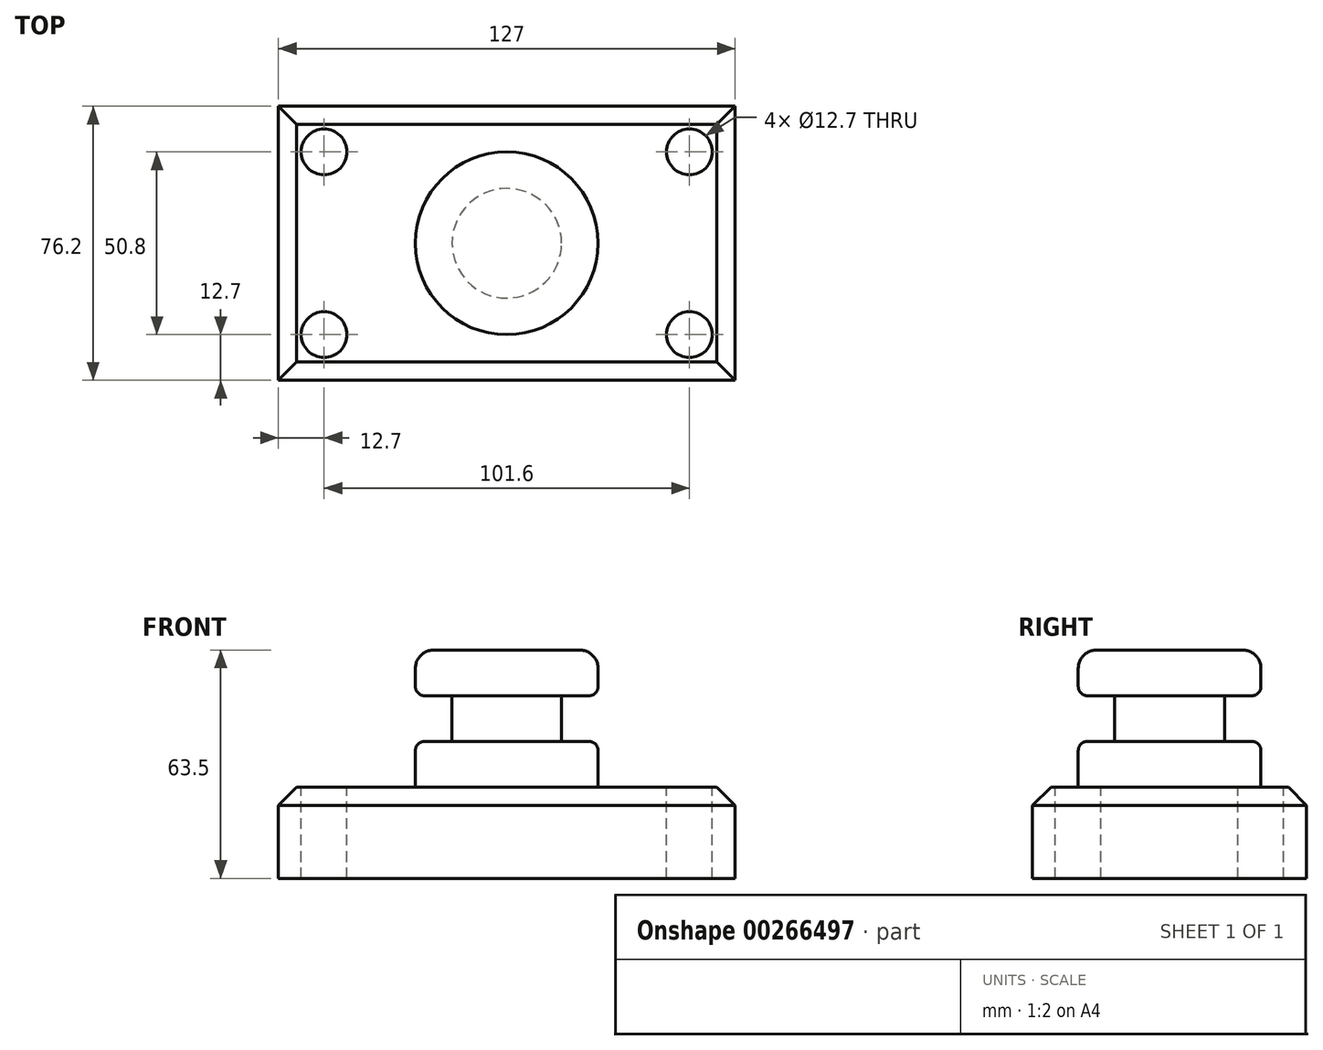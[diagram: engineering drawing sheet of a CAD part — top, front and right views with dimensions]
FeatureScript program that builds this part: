
annotation { "Feature Type Name" : "Feature", "Feature Type Description" : "" }
export const myFeature = defineFeature(function(context is Context, id is Id, definition is map)
    precondition{}
    {
        {
            var Q0;
            Q0=qCreatedBy(makeId("Top.planeOp"),FACE);
            var sketch = newSketch(context, id + "F0", { "sketchPlane" : qUnion([Q0])});
            skLineSegment(sketch, "E0.bottom", {"start": v(-63.5, -38.1) * mm, "end": v(63.5, -38.1) * mm});
            skLineSegment(sketch, "E0.top", {"start": v(-63.5, 38.1) * mm, "end": v(63.5, 38.1) * mm});
            skLineSegment(sketch, "E0.left", {"start": v(-63.5, 38.1) * mm, "end": v(-63.5, -38.1) * mm});
            skLineSegment(sketch, "E0.right", {"start": v(63.5, 38.1) * mm, "end": v(63.5, -38.1) * mm});
            skPoint(sketch, "E0.middle", {"position": v(0, 0) * mm});
            skSolve(sketch);
        }
        {
            var Q0;
            Q0=makeQuery(id+"F0.imprint","IMPRINT",FACE,{"disambiguationData":[TD([[makeQuery(id+"F0.imprint","IMPRINT",EDGE,{"derivedFrom":sQuery(id+"F0.wireOp",EDGE,"E0.bottom")}),1.0]])]});
            extrude(context, id + "F1", {"entities" : qUnion([Q0]), "depth" : 25.4 * mm});
        }
        {
            var Q0;
            Q0=makeQuery(id+"F1.opExtrude","CAP_FACE",FACE,{"disambiguationData":[OSD([sQuery(id+"F0.wireOp",EDGE,"E0.bottom"),sQuery(id+"F0.wireOp",EDGE,"E0.top"),sQuery(id+"F0.wireOp",EDGE,"E0.left"),sQuery(id+"F0.wireOp",EDGE,"E0.right")])],"isStart":false});
            var sketch = newSketch(context, id + "F2", { "sketchPlane" : qUnion([Q0])});
            skCircle(sketch, "E1", {"center": v(50.8, -25.4) * mm, "radius": 6.35 * mm});
            skCircle(sketch, "E2", {"center": v(50.8, 25.4) * mm, "radius": 6.35 * mm});
            skCircle(sketch, "E3", {"center": v(-50.8, 25.4) * mm, "radius": 6.35 * mm});
            skCircle(sketch, "E4", {"center": v(-50.8, -25.4) * mm, "radius": 6.35 * mm});
            skSolve(sketch);
        }
        {
            var Q0;
            Q0=makeQuery(id+"F2.imprint","IMPRINT",FACE,{"disambiguationData":[TD([[makeQuery(id+"F2.imprint","IMPRINT",EDGE,{"derivedFrom":sQuery(id+"F2.wireOp",EDGE,"E2")}),1.0]])]});
            var Q1;
            Q1=makeQuery(id+"F2.imprint","IMPRINT",FACE,{"disambiguationData":[TD([[makeQuery(id+"F2.imprint","IMPRINT",EDGE,{"derivedFrom":sQuery(id+"F2.wireOp",EDGE,"E1")}),1.0]])]});
            var Q2;
            Q2=makeQuery(id+"F2.imprint","IMPRINT",FACE,{"disambiguationData":[TD([[makeQuery(id+"F2.imprint","IMPRINT",EDGE,{"derivedFrom":sQuery(id+"F2.wireOp",EDGE,"E4")}),1.0]])]});
            var Q3;
            Q3=makeQuery(id+"F2.imprint","IMPRINT",FACE,{"disambiguationData":[TD([[makeQuery(id+"F2.imprint","IMPRINT",EDGE,{"derivedFrom":sQuery(id+"F2.wireOp",EDGE,"E3")}),1.0]])]});
            extrude(context, id + "F3", {"entities" : qUnion([Q0, Q1, Q2, Q3]), "operationType" : NewBodyOperationType.REMOVE, "endBound" : BoundingType.THROUGH_ALL, "oppositeDirection" : true, "depth" : 25.4 * mm});
        }
        {
            var Q0;
            Q0=qCreatedBy(makeId("Front.planeOp"),FACE);
            var sketch = newSketch(context, id + "F4", { "sketchPlane" : qUnion([Q0])});
            skLineSegment(sketch, "E5.bottom", {"start": v(0, 25.4) * mm, "end": v(-25.4, 25.4) * mm});
            skLineSegment(sketch, "E5.top", {"start": v(0, 63.5) * mm, "end": v(-25.4, 63.5) * mm});
            skLineSegment(sketch, "E5.left", {"start": v(0, 25.4) * mm, "end": v(0, 63.5) * mm});
            skLineSegment(sketch, "E5.right", {"start": v(-25.4, 25.4) * mm, "end": v(-25.4, 63.5) * mm});
            skSolve(sketch);
        }
        {
            var Q0;
            Q0=makeQuery(id+"F4.imprint","IMPRINT",FACE,{"disambiguationData":[TD([[makeQuery(id+"F4.imprint","IMPRINT",EDGE,{"derivedFrom":sQuery(id+"F4.wireOp",EDGE,"E5.bottom")}),-1.0]])]});
            var Q1;
            Q1=sQuery(id+"F4.wireOp",EDGE,"E5.left");
            revolve(context, id + "F5", {"operationType" : NewBodyOperationType.ADD, "entities" : qUnion([Q0]), "axis" : qUnion([Q1]), "revolveType" : RevolveType.FULL});
        }
        {
            var Q0;
            Q0=qCreatedBy(makeId("Front.planeOp"),FACE);
            var sketch = newSketch(context, id + "F6", { "sketchPlane" : qUnion([Q0])});
            skLineSegment(sketch, "E6.bottom", {"start": v(-40.64, 50.8) * mm, "end": v(-15.24, 50.8) * mm});
            skLineSegment(sketch, "E6.top", {"start": v(-40.64, 38.1) * mm, "end": v(-15.24, 38.1) * mm});
            skLineSegment(sketch, "E6.left", {"start": v(-40.64, 50.8) * mm, "end": v(-40.64, 38.1) * mm});
            skLineSegment(sketch, "E6.right", {"start": v(-15.24, 50.8) * mm, "end": v(-15.24, 38.1) * mm});
            skSolve(sketch);
        }
        {
            var Q0;
            Q0=makeQuery(id+"F6.imprint","IMPRINT",FACE,{"disambiguationData":[TD([[makeQuery(id+"F6.imprint","IMPRINT",EDGE,{"derivedFrom":sQuery(id+"F6.wireOp",EDGE,"E6.bottom")}),-1.0]])]});
            var Q1;
            Q1=makeQuery(id+"F5.opRevolve","SWEPT_FACE",FACE,{"disambiguationData":[OSD([sQuery(id+"F4.wireOp",EDGE,"E5.right")])]});
            revolve(context, id + "F7", {"operationType" : NewBodyOperationType.REMOVE, "entities" : qUnion([Q0]), "axis" : qUnion([Q1]), "revolveType" : RevolveType.FULL, "oppositeDirection" : true});
        }
        {
            var Q0;
            Q0=makeQuery(id+"F1.opExtrude","CAP_EDGE",EDGE,{"disambiguationData":[OSD([sQuery(id+"F0.wireOp",EDGE,"E0.right")])],"isStart":false});
            var Q1;
            Q1=makeQuery(id+"F1.opExtrude","CAP_EDGE",EDGE,{"disambiguationData":[OSD([sQuery(id+"F0.wireOp",EDGE,"E0.top")])],"isStart":false});
            var Q2;
            Q2=makeQuery(id+"F1.opExtrude","CAP_EDGE",EDGE,{"disambiguationData":[OSD([sQuery(id+"F0.wireOp",EDGE,"E0.left")])],"isStart":false});
            var Q3;
            Q3=makeQuery(id+"F1.opExtrude","CAP_EDGE",EDGE,{"disambiguationData":[OSD([sQuery(id+"F0.wireOp",EDGE,"E0.bottom")])],"isStart":false});
            chamfer(context, id + "F8", {"entities" : qUnion([Q0, Q1, Q2, Q3]), "width" : 5.08 * mm, "tangentPropagation" : true});
        }
        {
            var Q0;
            Q0=makeQuery(id+"F7.boolean.opBoolean","INTERSECT",EDGE,{"derivedFrom":[makeQuery(id+"F5.opRevolve","SWEPT_FACE",FACE,{"disambiguationData":[OSD([sQuery(id+"F4.wireOp",EDGE,"E5.right")])]}),makeQuery(id+"F7.opRevolve","SWEPT_FACE",FACE,{"disambiguationData":[OSD([sQuery(id+"F6.wireOp",EDGE,"E6.top")])]})]});
            var Q1;
            Q1=makeQuery(id+"F5.opRevolve","SWEPT_EDGE",EDGE,{"disambiguationData":[OSD([sQuery(id+"F4.wireOp",EDGE,"E5.bottom"),sQuery(id+"F4.wireOp",EDGE,"E5.right")])]});
            var Q2;
            Q2=makeQuery(id+"F7.boolean.opBoolean","INTERSECT",EDGE,{"derivedFrom":[makeQuery(id+"F5.opRevolve","SWEPT_FACE",FACE,{"disambiguationData":[OSD([sQuery(id+"F4.wireOp",EDGE,"E5.right")])]}),makeQuery(id+"F7.opRevolve","SWEPT_FACE",FACE,{"disambiguationData":[OSD([sQuery(id+"F6.wireOp",EDGE,"E6.bottom")])]})]});
            fillet(context, id + "F9", {"entities" : qUnion([Q0, Q1, Q2]), "radius" : 2.54 * mm, "tangentPropagation" : true, "allowEdgeOverflow" : false});
        }
        {
            var Q0;
            Q0=makeQuery(id+"F5.opRevolve","SWEPT_EDGE",EDGE,{"disambiguationData":[OSD([sQuery(id+"F4.wireOp",EDGE,"E5.top"),sQuery(id+"F4.wireOp",EDGE,"E5.right")])]});
            fillet(context, id + "F10", {"entities" : qUnion([Q0]), "radius" : 5.08 * mm, "tangentPropagation" : true, "allowEdgeOverflow" : false});
        }
    });
